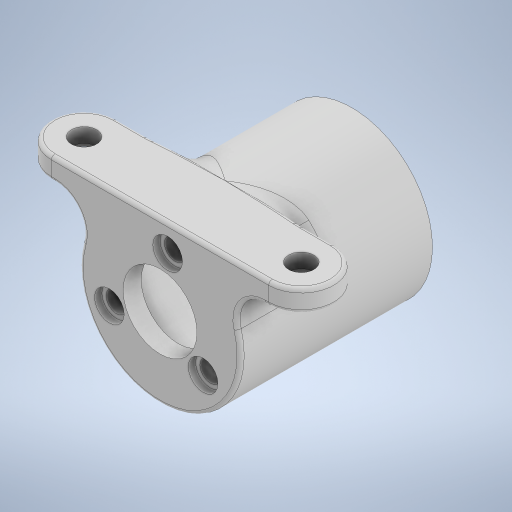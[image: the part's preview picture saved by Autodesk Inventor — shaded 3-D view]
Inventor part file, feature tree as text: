
AUTODESK INVENTOR PART (.ipt)
format: ipt  version: 2024.2 (Build 282272000, 272)  size: 422,400 bytes
history: native  units: mm
features: sketch x7, extrude x5, hole x2, fillet x2, plane x1, chamfer x1
ambient origin geometry x8: Origin, YZ Plane, XZ Plane, XY Plane, X Axis, Y Axis, Z Axis, Center Point
bodies: Solid1 (feature_tree)
feature tree (18):
  extrude  "Extrusion1"  Depth=2.9mm
  extrude  "Extrusion2"  Depth=30.0mm TaperAngle=360.0deg
  extrude  "Extrusion3"  Depth=22.25mm
  plane  "Work Plane1"
  extrude  "Extrusion4"  Depth=4.1mm
  extrude  "Extrusion5"  Depth=20.25mm
  hole  "Hole1"  [1 undecoded]
  hole  "Hole2"  [1 undecoded]
  fillet  "Fillet1"  Radius=15.0mm
  fillet  "Fillet2"  Radius=3.0mm
  chamfer  "Chamfer1"  Distance=1.5mm
  sketch  "Sketch1"  dims[d0=10.2mm d1=2.9mm]
  sketch  "Sketch2"  dims[d2=7.55mm d3=30.0mm d5=360.0deg]
  sketch  "Sketch3"  dims[d7=1.396263mm d8=22.25mm]
  sketch  "Sketch4"  dims[d9=1.5mm d10=0.0mm d11=4.1mm]
  sketch  "Sketch5"  dims[d12=1.0mm d13=0.0mm d14=20.25mm]
  sketch  "Sketch6"  dims[d15=24.0mm d16=0.0mm d17=11.125mm]
  sketch  "Sketch7"  dims[d18=9.0mm d19=30.0mm d20=15.0mm d21=3.0mm d22=0.0mm d23=1.5mm d24=0.0mm d25=2.9mm d26=6.0mm d27=4.1mm d28=1.0mm d29=90.0deg d30=8.0mm d31=20.594885mm d32=3.5mm d33=6.0mm d34=5.25mm d35=1.0mm d36=90.0deg d37=8.0mm d38=20.594885mm d39=4.0mm d40=0.5mm d41=0.5mm d42=2.0mm d43=45.0deg]
note: 2 required parameter values undecoded (feature->parameter linkage not recoverable at this tier; creation-order binding heuristic only, values carry confidence <= 0.55)
